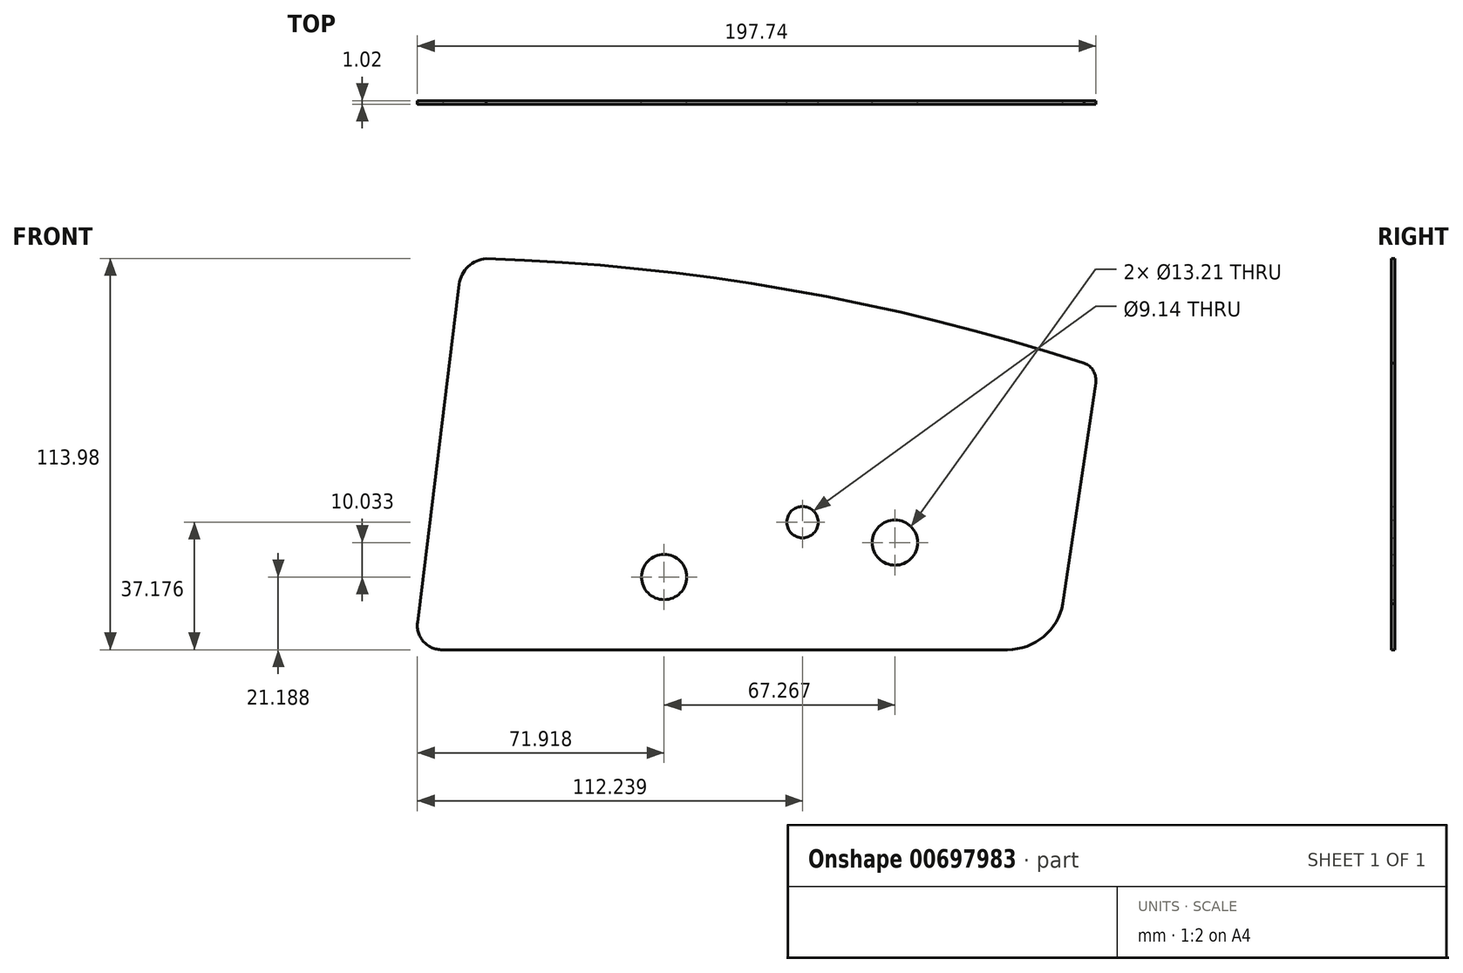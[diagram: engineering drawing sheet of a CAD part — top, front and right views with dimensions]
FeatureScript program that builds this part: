
annotation { "Feature Type Name" : "Feature", "Feature Type Description" : "" }
export const myFeature = defineFeature(function(context is Context, id is Id, definition is map)
    precondition{}
    {
        {
            var Q0;
            Q0=qCreatedBy(makeId("Front.planeOp"),FACE);
            var sketch = newSketch(context, id + "F0", { "sketchPlane" : qUnion([Q0])});
            skCircle(sketch, "E0", {"center": v(12, -11.53) * mm, "radius": 4.57 * mm});
            skCircle(sketch, "E1", {"center": v(12, -11.53) * mm, "radius": 6.1 * mm});
            skCircle(sketch, "E2", {"center": v(38.95, -17.49) * mm, "radius": 5.08 * mm});
            skCircle(sketch, "E3", {"center": v(38.95, -17.49) * mm, "radius": 6.6 * mm});
            skCircle(sketch, "E4", {"center": v(-28.32, -27.52) * mm, "radius": 6.6 * mm});
            skPoint(sketch, "E4.centerSnap0", {"position": v(-8.67, -19.76) * mm});
            skCircle(sketch, "E5", {"center": v(-28.32, -27.52) * mm, "radius": 5.08 * mm});
            skLineSegment(sketch, "E6", {"start": v(87.88, -35.3) * mm, "end": v(97.44, 29.05) * mm});
            skLineSegment(sketch, "E7", {"start": v(-88.04, 57.8) * mm, "end": v(-100.19, -40.73) * mm});
            skLineSegment(sketch, "E8", {"start": v(-92.64, -48.7) * mm, "end": v(71.75, -48.7) * mm});
            skArc(sketch, "E9", {"start": v(71.75, -48.7) * mm, "mid": v(82.23, -44.9) * mm, "end": v(87.88, -35.3) * mm});
            skArc(sketch, "E10", {"start": v(94.11, 34.8) * mm, "mid": v(8.06, 56.2) * mm, "end": v(-80.14, 65.27) * mm});
            skArc(sketch, "E11", {"start": v(-80.14, 65.27) * mm, "mid": v(-85.44, 62.95) * mm, "end": v(-88.04, 57.8) * mm});
            skArc(sketch, "E12", {"start": v(97.44, 29.05) * mm, "mid": v(96.78, 32.5) * mm, "end": v(94.11, 34.8) * mm});
            skArc(sketch, "E13", {"start": v(-100.19, -40.73) * mm, "mid": v(-98.3, -46.5) * mm, "end": v(-92.64, -48.7) * mm});
            skCircle(sketch, "E14", {"center": v(12, -11.53) * mm, "radius": 11.6 * mm});
            skArc(sketch, "E15.0", {"start": v(77, 25.25) * mm, "mid": v(4.94, 42.3) * mm, "end": v(-68.66, 50.56) * mm});
            skLineSegment(sketch, "E16.0", {"start": v(-75.29, 45) * mm, "end": v(-84.64, -30.9) * mm});
            skLineSegment(sketch, "E17.0", {"start": v(-81.5, -34.47) * mm, "end": v(-9.8, -34.47) * mm});
            skLineSegment(sketch, "E18.0", {"start": v(74.02, -31.76) * mm, "end": v(81.45, 18.24) * mm});
            skArc(sketch, "E19", {"start": v(-6.05, -35.7) * mm, "mid": v(11.86, -41.58) * mm, "end": v(29.78, -35.7) * mm});
            skLineSegment(sketch, "E20.trimOffspring", {"start": v(33.54, -34.47) * mm, "end": v(70.88, -34.47) * mm});
            skPoint(sketch, "E21.visualSharp", {"position": v(31.34, -34.47) * mm});
            skArc(sketch, "E21.filletArc", {"start": v(33.54, -34.47) * mm, "mid": v(31.56, -34.79) * mm, "end": v(29.78, -35.7) * mm});
            skPoint(sketch, "E22.visualSharp", {"position": v(-7.62, -34.47) * mm});
            skArc(sketch, "E22.filletArc", {"start": v(-6.05, -35.7) * mm, "mid": v(-7.83, -34.79) * mm, "end": v(-9.8, -34.47) * mm});
            skPoint(sketch, "E23.visualSharp", {"position": v(73.62, -34.47) * mm});
            skArc(sketch, "E23.filletArc", {"start": v(70.88, -34.47) * mm, "mid": v(72.96, -33.7) * mm, "end": v(74.02, -31.76) * mm});
            skPoint(sketch, "E24.visualSharp", {"position": v(82.26, 23.64) * mm});
            skArc(sketch, "E24.filletArc", {"start": v(81.45, 18.24) * mm, "mid": v(80.53, 22.57) * mm, "end": v(77, 25.25) * mm});
            skPoint(sketch, "E25.visualSharp", {"position": v(-74.57, 50.83) * mm});
            skArc(sketch, "E25.filletArc", {"start": v(-68.66, 50.56) * mm, "mid": v(-73.07, 49.08) * mm, "end": v(-75.29, 45) * mm});
            skPoint(sketch, "E26.visualSharp", {"position": v(-85.08, -34.47) * mm});
            skArc(sketch, "E26.filletArc", {"start": v(-84.64, -30.9) * mm, "mid": v(-83.87, -33.4) * mm, "end": v(-81.5, -34.47) * mm});
            skSolve(sketch);
        }
        {
            var Q0;
            Q0=makeQuery(id+"F0.imprint","IMPRINT",FACE,{"disambiguationData":[TD([[makeQuery(id+"F0.imprint","IMPRINT",EDGE,{"derivedFrom":sQuery(id+"F0.wireOp",EDGE,"E6")}),1.0]])]});
            extrude(context, id + "F1", {"entities" : qUnion([Q0]), "depth" : 1.02 * mm, "offsetDistance" : 25.4 * mm});
        }
        {
            var Q0;
            Q0=makeQuery(id+"F0.imprint","IMPRINT",FACE,{"disambiguationData":[TD([[makeQuery(id+"F0.imprint","IMPRINT",EDGE,{"derivedFrom":sQuery(id+"F0.wireOp",EDGE,"E3")}),-1.0]])]});
            var Q1;
            Q1=makeQuery(id+"F0.imprint","IMPRINT",FACE,{"disambiguationData":[TD([[makeQuery(id+"F0.imprint","IMPRINT",EDGE,{"derivedFrom":sQuery(id+"F0.wireOp",EDGE,"E1")}),-1.0]])]});
            var Q2;
            Q2=makeQuery(id+"F0.imprint","IMPRINT",FACE,{"disambiguationData":[TD([[makeQuery(id+"F0.imprint","IMPRINT",EDGE,{"derivedFrom":sQuery(id+"F0.wireOp",EDGE,"E0")}),-1.0]])]});
            extrude(context, id + "F2", {"entities" : qUnion([Q0, Q1, Q2]), "operationType" : NewBodyOperationType.ADD, "depth" : 1.02 * mm, "offsetDistance" : 25.4 * mm});
        }
    });
